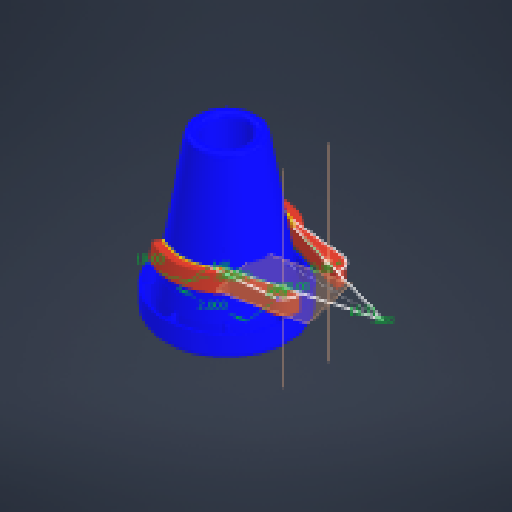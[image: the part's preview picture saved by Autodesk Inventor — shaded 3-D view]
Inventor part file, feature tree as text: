
AUTODESK INVENTOR PART (.ipt)
format: ipt  version: 2024.2 (Build 282272000, 272)  size: 3,276,800 bytes
history: native  units: in
note: dims shown in document units (in); Inventor stores cm internally (conversion verified against a paired STEP export)
features: other x10, sketch x8, reference x7, plane x5, extrude x4, projected_geometry x3, revolve x1, fillet x1
ambient origin geometry x8: Origin, YZ Plane, XZ Plane, XY Plane, X Axis, Y Axis, Z Axis, Center Point
bodies: Solid1 (feature_tree)
feature tree (39):
  other  "am-4801_Blue am-4801_Red Cone REV2.STEP"
  plane  "Work Plane2"
  sketch  "Sketch1"  dims[d1=1.0in d2=0.1in]
  plane  "Work Plane3"
  sketch  "Sketch2"  dims[d3=0.0in d4=30.0deg]
  sketch  "3D Sketch1"
  plane  "Work Plane4"
  revolve  "Revolution1"  [1 undecoded]
  extrude  "Extrusion1"  TaperAngle=30.0deg  [1 undecoded]
  extrude  "Extrusion2"  Depth=0.25in
  other  "Work Point1"
  other  "Work Point2"
  other  "Work Axis1"
  other  "Work Axis2"
  plane  "Work Plane5"
  extrude  "Extrusion3"  Depth=0.1in
  plane  "Work Plane6"
  extrude  "Extrusion4"  TaperAngle=240.0deg  [1 undecoded]
  projected_geometry  "Projected Loop1"
  projected_geometry  "Projected Loop2"
  sketch  "Sketch3"  dims[d5=30.0deg d7=0.25in]
  sketch  "Sketch4"  dims[d8=0.5in d9=0.1in]
  sketch  "Sketch5"  dims[d10=0.25in d11=240.0deg d12=0.0in]
  sketch  "Sketch6"  dims[d13=5.0in]
  sketch  "Sketch7"  dims[d14=1.0in d15=1.0in d16=0.0in d18=0.0687in d21=0.2in d22=0.0in d23=0.1397in d24=0.2091in d25=2.0in d26=0.0in d27=0.0in d28=0.0in d29=0.1079in d30=0.0in d31=0.85in d32=1.0in d33=0.0in d34=1.0in d35=0.0in d36=1.0in d37=0.0in d17=0.5in]
  reference  "Reference1"
  reference  "Reference2"
  reference  "Reference3"
  reference  "Reference4"
  reference  "Reference5"
  reference  "Reference6"
  reference  "Reference7"
  fillet  "Fillet23"  [1 undecoded]
  projected_geometry  "Project Cut Edges1"
  other  "<userpath>\Desktop\Robotics\Cad\Powerplay_Fun\Parts\Claw_Assembly.iam"
  other  "Claw_Assembly.iam"
  other  "Spur Gears:1"
  other  "Spur Gear2:1"
  other  "Spur Gear1:1"
note: 4 required parameter values undecoded (feature->parameter linkage not recoverable at this tier; creation-order binding heuristic only, values carry confidence <= 0.55)